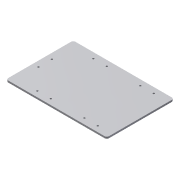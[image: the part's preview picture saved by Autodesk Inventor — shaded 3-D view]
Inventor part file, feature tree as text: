
AUTODESK INVENTOR PART (.ipt)
format: ipt  version: 2014 (Build 180170000, 170)  size: 154,624 bytes
history: native  units: mm
features: extrude x3, sketch x3, fillet x1
ambient origin geometry x8: Origin, YZ Plane, XZ Plane, XY Plane, X Axis, Y Axis, Z Axis, Center Point
bodies: Solid1 (feature_tree)
feature tree (7):
  extrude  "Extrusion1"  Depth=100.0mm
  extrude  "Extrusion2"  Depth=4.0mm
  extrude  "Extrusion3"  Depth=5.0mm
  fillet  "Fillet1"  Radius=30.0mm
  sketch  "Sketch1"  dims[d0=200.0mm d1=100.0mm]
  sketch  "Sketch2"  dims[d2=4.0mm d3=0.0mm d6=45.0mm]
  sketch  "Sketch3"  dims[d8=30.0mm d9=30.0mm d11=30.0mm d13=25.0mm d14=7.5mm d15=7.5mm d16=50.0mm d17=10.0mm d18=12.5mm d19=4.0mm d20=12.5mm d21=12.5mm d22=4.0mm d23=0.0mm d24=4.0mm d25=0.0mm d26=5.0mm]
